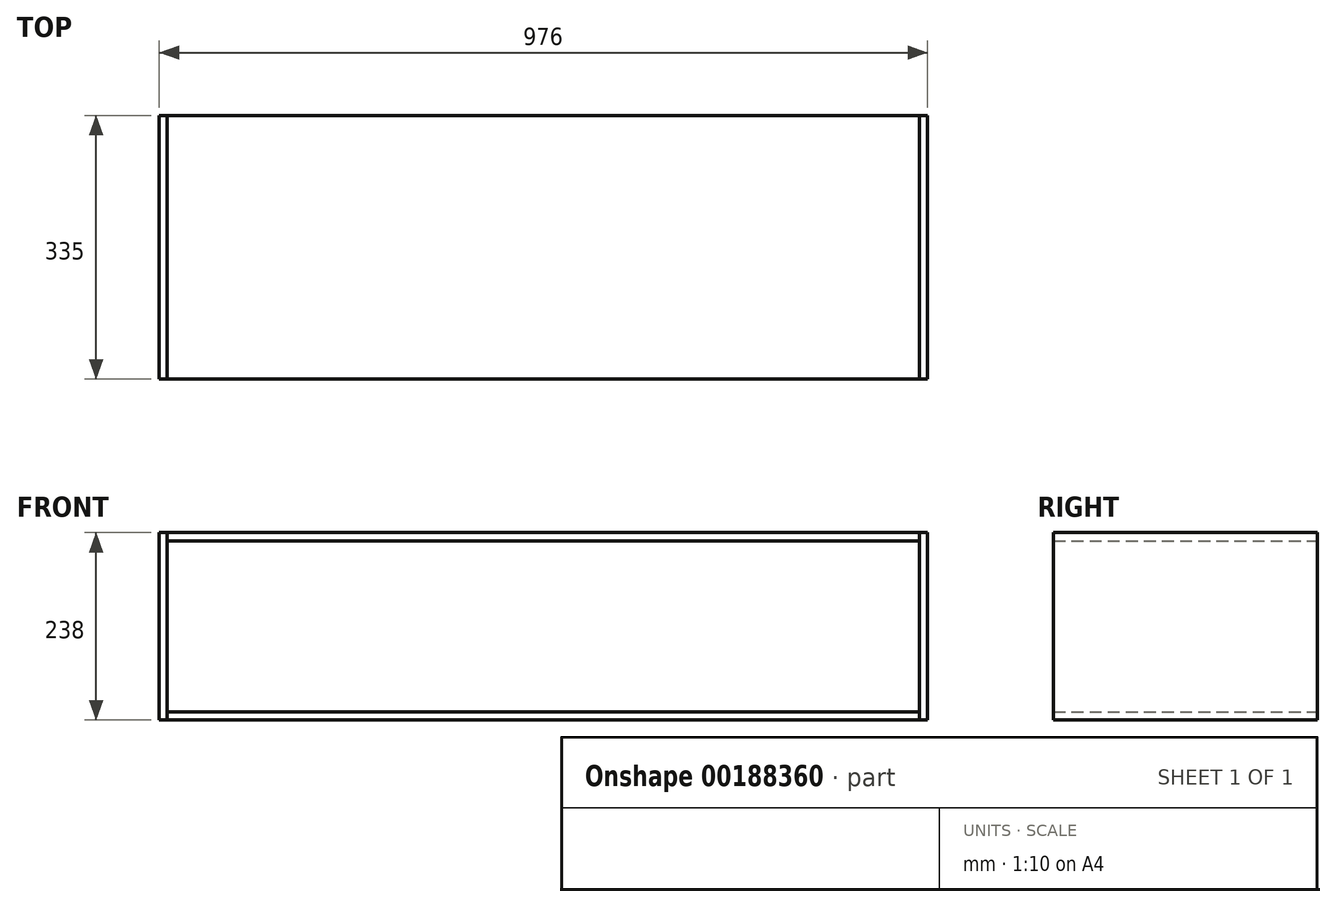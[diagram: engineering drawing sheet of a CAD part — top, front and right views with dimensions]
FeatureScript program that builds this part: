
annotation { "Feature Type Name" : "Feature", "Feature Type Description" : "" }
export const myFeature = defineFeature(function(context is Context, id is Id, definition is map)
    precondition{}
    {
        {
            var Q0;
            Q0=qCreatedBy(makeId("Front.planeOp"),FACE);
            var sketch = newSketch(context, id + "F0", { "sketchPlane" : qUnion([Q0])});
            skLineSegment(sketch, "E0.bottom", {"start": v(488, -119) * mm, "end": v(-488, -119) * mm});
            skLineSegment(sketch, "E0.top", {"start": v(488, 119) * mm, "end": v(-488, 119) * mm});
            skLineSegment(sketch, "E0.left", {"start": v(488, -119) * mm, "end": v(488, 119) * mm});
            skLineSegment(sketch, "E0.right", {"start": v(-488, -119) * mm, "end": v(-488, 119) * mm});
            skPoint(sketch, "E0.middle", {"position": v(0, 0) * mm});
            skLineSegment(sketch, "E1.0", {"start": v(477.6, 108.6) * mm, "end": v(-477.6, 108.6) * mm});
            skLineSegment(sketch, "E1.1", {"start": v(477.6, -108.6) * mm, "end": v(477.6, 108.6) * mm});
            skLineSegment(sketch, "E1.2", {"start": v(477.6, -108.6) * mm, "end": v(-477.6, -108.6) * mm});
            skLineSegment(sketch, "E1.3", {"start": v(-477.6, -108.6) * mm, "end": v(-477.6, 108.6) * mm});
            skLineSegment(sketch, "E2", {"start": v(-477.6, 108.6) * mm, "end": v(-477.6, 119) * mm});
            skLineSegment(sketch, "E3.MirrorCS", {"start": v(477.6, 108.6) * mm, "end": v(477.6, 119) * mm});
            skLineSegment(sketch, "E4.MirrorCS", {"start": v(477.6, -108.6) * mm, "end": v(477.6, -119) * mm});
            skLineSegment(sketch, "E5.MirrorCS", {"start": v(-477.6, -108.6) * mm, "end": v(-477.6, -119) * mm});
            skSolve(sketch);
        }
        {
            var Q0;
            Q0=makeQuery(id+"F0.imprint","IMPRINT",FACE,{"disambiguationData":[TD([[makeQuery(id+"F0.imprint","IMPRINT",EDGE,{"derivedFrom":sQuery(id+"F0.wireOp",EDGE,"E1.2")}),1.0]])]});
            var Q1;
            Q1=makeQuery(id+"F0.imprint","IMPRINT",FACE,{"disambiguationData":[TD([[makeQuery(id+"F0.imprint","IMPRINT",EDGE,{"derivedFrom":sQuery(id+"F0.wireOp",EDGE,"E1.0")}),-1.0]])]});
            extrude(context, id + "F1", {"entities" : qUnion([Q0, Q1]), "depth" : 335 * mm});
        }
        {
            var Q0;
            {var subQ0=sQuery(id+"F0.wireOp",EDGE,"E0.right");Q0=makeQuery(id+"F0.imprint","IMPRINT",FACE,{"disambiguationData":[TD([[makeQuery(id+"F0.imprint","IMPRINT",EDGE,{"derivedFrom":subQ0}),-1.0]])]});}
            var Q1;
            {var subQ0=sQuery(id+"F0.wireOp",EDGE,"E0.left");Q1=makeQuery(id+"F0.imprint","IMPRINT",FACE,{"disambiguationData":[TD([[makeQuery(id+"F0.imprint","IMPRINT",EDGE,{"derivedFrom":subQ0}),1.0]])]});}
            var Q2;
            Q2=makeQuery(id+"F1.opExtrude","CAP_VERTEX",VERTEX,{"disambiguationData":[OSD([sQuery(id+"F0.wireOp",EDGE,"E1.0"),sQuery(id+"F0.wireOp",EDGE,"E1.3"),sQuery(id+"F0.wireOp",EDGE,"E2")])],"isStart":false});
            extrude(context, id + "F2", {"entities" : qUnion([Q0, Q1]), "endBound" : BoundingType.UP_TO_VERTEX, "endBoundEntityVertex" : qUnion([Q2]), "depth" : 25 * mm});
        }
    });
